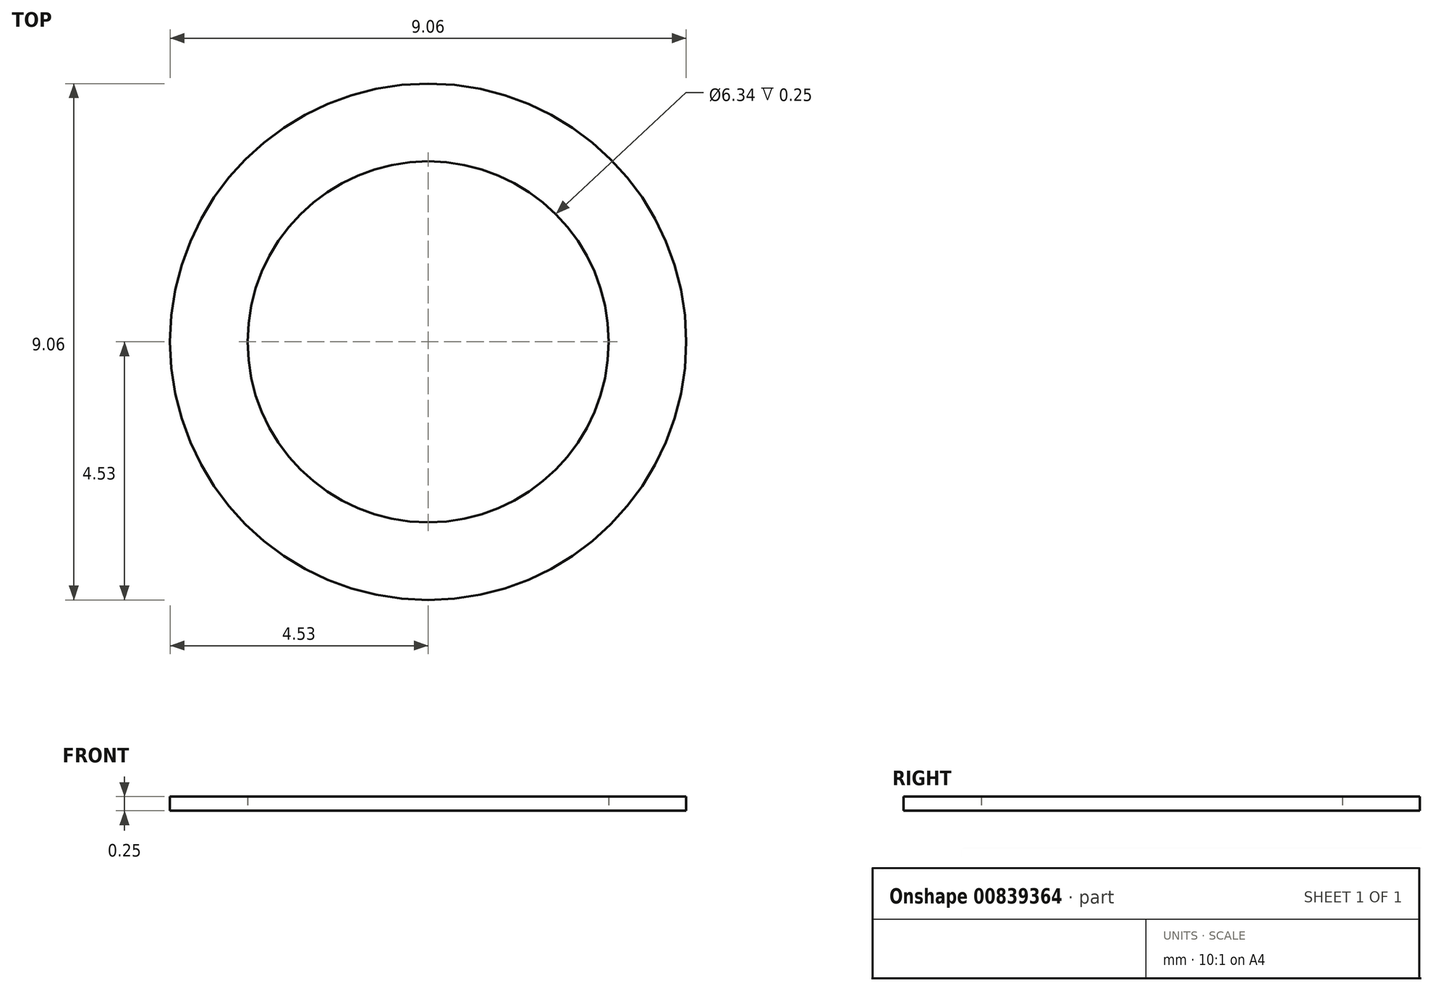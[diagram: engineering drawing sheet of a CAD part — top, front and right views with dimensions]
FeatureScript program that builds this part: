
annotation { "Feature Type Name" : "Feature", "Feature Type Description" : "" }
export const myFeature = defineFeature(function(context is Context, id is Id, definition is map)
    precondition{}
    {
        {
            var Q0;
            Q0=qCreatedBy(makeId("Top.planeOp"),FACE);
            var sketch = newSketch(context, id + "F0", { "sketchPlane" : qUnion([Q0])});
            skCircle(sketch, "E0", {"center": v(0, 0) * mm, "radius": 4.53 * mm});
            skCircle(sketch, "E1", {"center": v(0, 0) * mm, "radius": 3.17 * mm});
            skSolve(sketch);
        }
        {
            var Q0;
            Q0=makeQuery(id+"F0.imprint","IMPRINT",FACE,{"disambiguationData":[TD([[makeQuery(id+"F0.imprint","IMPRINT",EDGE,{"derivedFrom":sQuery(id+"F0.wireOp",EDGE,"E0")}),1.0]])]});
            extrude(context, id + "F1", {"entities" : qUnion([Q0]), "depth" : 0.25 * mm, "offsetDistance" : 25.4 * mm});
        }
    });
